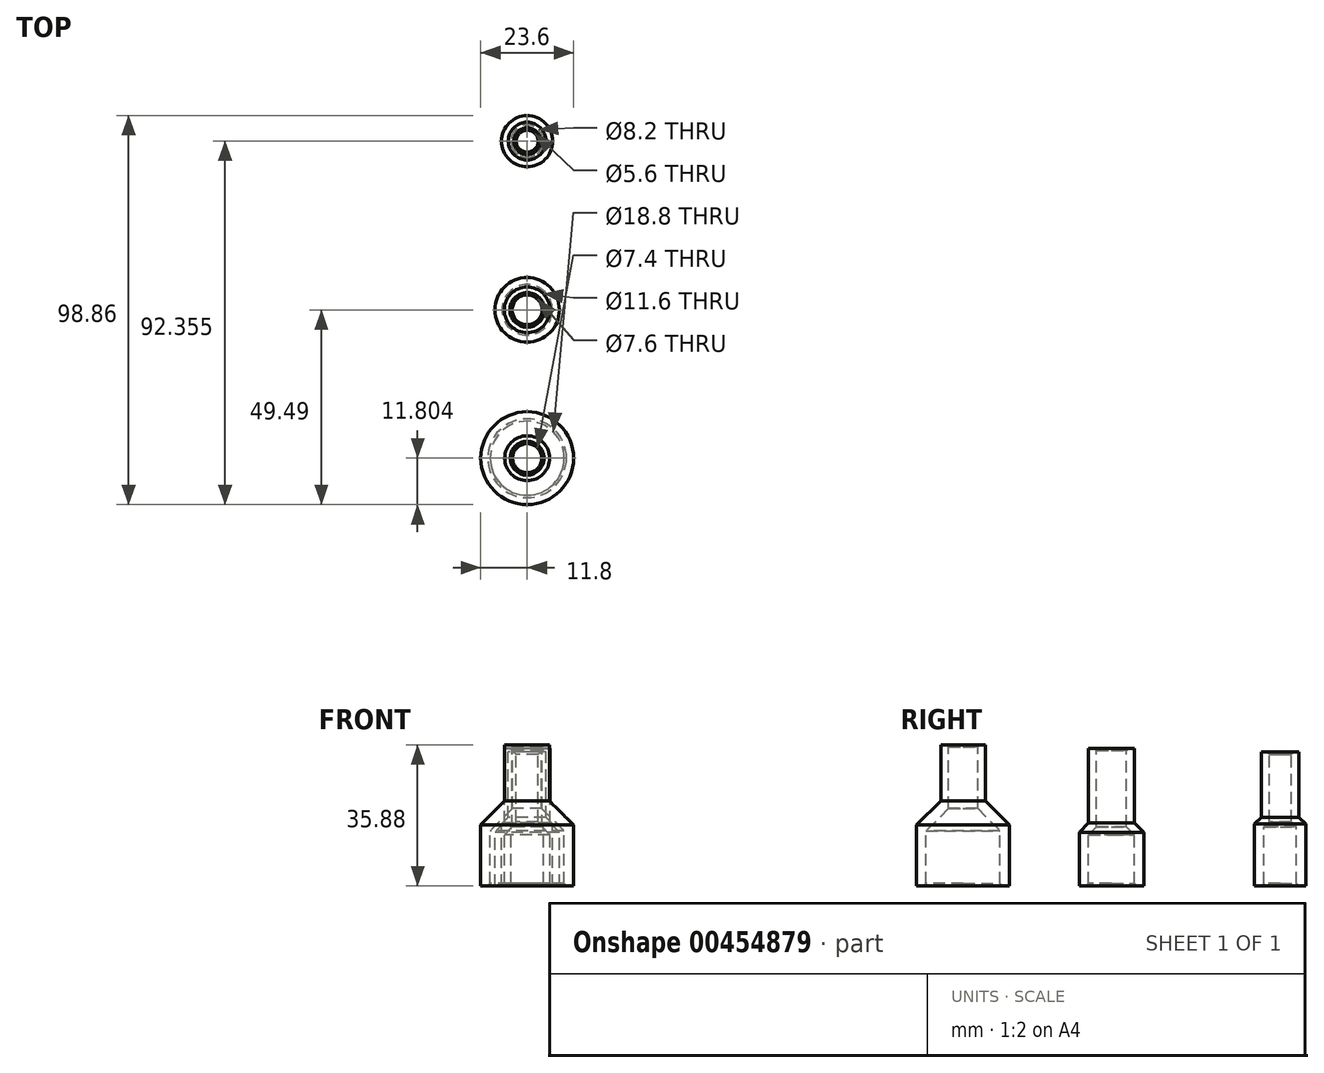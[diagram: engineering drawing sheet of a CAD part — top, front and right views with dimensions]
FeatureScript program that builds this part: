
annotation { "Feature Type Name" : "Feature", "Feature Type Description" : "" }
export const myFeature = defineFeature(function(context is Context, id is Id, definition is map)
    precondition{}
    {
        {
            var Q0;
            Q0=qCreatedBy(makeId("Right.planeOp"),FACE);
            var sketch = newSketch(context, id + "F0", { "sketchPlane" : qUnion([Q0])});
            skLineSegment(sketch, "E0", {"start": v(0, 29.48) * mm, "end": v(0, -19) * mm, "construction": true});
            skLineSegment(sketch, "E1", {"start": v(-5.8, 0) * mm, "end": v(-5.8, 13) * mm});
            skLineSegment(sketch, "E2", {"start": v(-5.8, 13) * mm, "end": v(-3.8, 15) * mm});
            skLineSegment(sketch, "E3", {"start": v(-3.8, 15) * mm, "end": v(-3.8, 34.98) * mm});
            skLineSegment(sketch, "E4", {"start": v(-3.8, 34.98) * mm, "end": v(-5.8, 34.98) * mm});
            skLineSegment(sketch, "E5", {"start": v(-5.8, 34.98) * mm, "end": v(-5.8, 16.05) * mm});
            skLineSegment(sketch, "E6", {"start": v(-5.8, 16.05) * mm, "end": v(-8.2, 13.65) * mm});
            skLineSegment(sketch, "E7", {"start": v(-8.2, 13.65) * mm, "end": v(-8.2, 0) * mm});
            skLineSegment(sketch, "E8", {"start": v(-8.2, 0) * mm, "end": v(-5.8, 0) * mm});
            skLineSegment(sketch, "E9", {"start": v(42.87, 33.76) * mm, "end": v(42.87, -16.37) * mm, "construction": true});
            skLineSegment(sketch, "E10", {"start": v(38.77, 0) * mm, "end": v(38.77, 15) * mm});
            skLineSegment(sketch, "E11", {"start": v(38.77, 15) * mm, "end": v(40.07, 16.3) * mm});
            skLineSegment(sketch, "E12", {"start": v(40.07, 16.3) * mm, "end": v(40.07, 34.07) * mm});
            skLineSegment(sketch, "E13", {"start": v(40.07, 34.07) * mm, "end": v(38.07, 34.07) * mm});
            skLineSegment(sketch, "E14", {"start": v(38.07, 34.07) * mm, "end": v(38.07, 17.4) * mm});
            skLineSegment(sketch, "E15", {"start": v(38.07, 17.4) * mm, "end": v(36.37, 15.7) * mm});
            skLineSegment(sketch, "E16", {"start": v(36.37, 15.7) * mm, "end": v(36.37, 0) * mm});
            skLineSegment(sketch, "E17", {"start": v(36.37, 0) * mm, "end": v(38.77, 0) * mm});
            skLineSegment(sketch, "E18", {"start": v(-47.09, 0) * mm, "end": v(-47.09, 14) * mm});
            skLineSegment(sketch, "E19", {"start": v(-47.09, 14) * mm, "end": v(-41.39, 19.7) * mm});
            skLineSegment(sketch, "E20", {"start": v(-41.39, 19.7) * mm, "end": v(-41.39, 35.88) * mm});
            skLineSegment(sketch, "E21", {"start": v(-41.39, 35.88) * mm, "end": v(-43.39, 35.88) * mm});
            skLineSegment(sketch, "E22", {"start": v(-43.39, 35.88) * mm, "end": v(-43.39, 21.58) * mm});
            skLineSegment(sketch, "E23", {"start": v(-43.39, 21.58) * mm, "end": v(-49.49, 15.48) * mm});
            skLineSegment(sketch, "E24", {"start": v(-49.49, 15.48) * mm, "end": v(-49.49, 0) * mm});
            skLineSegment(sketch, "E25", {"start": v(-49.49, 0) * mm, "end": v(-47.09, 0) * mm});
            skLineSegment(sketch, "E26", {"start": v(-37.69, 38.7) * mm, "end": v(-37.69, -6.54) * mm, "construction": true});
            skSolve(sketch);
        }
        {
            var Q0;
            Q0=makeQuery(id+"F0.imprint","IMPRINT",FACE,{"disambiguationData":[TD([[makeQuery(id+"F0.imprint","IMPRINT",EDGE,{"derivedFrom":sQuery(id+"F0.wireOp",EDGE,"E1")}),1.0]])]});
            var Q1;
            Q1=sQuery(id+"F0.wireOp",EDGE,"E0");
            revolve(context, id + "F1", {"entities" : qUnion([Q0]), "axis" : qUnion([Q1]), "revolveType" : RevolveType.FULL});
        }
        {
            var Q0;
            Q0=makeQuery(id+"F0.imprint","IMPRINT",FACE,{"disambiguationData":[TD([[makeQuery(id+"F0.imprint","IMPRINT",EDGE,{"derivedFrom":sQuery(id+"F0.wireOp",EDGE,"E10")}),1.0]])]});
            var Q1;
            Q1=sQuery(id+"F0.wireOp",EDGE,"E9");
            revolve(context, id + "F2", {"surfaceOperationType" : NewSurfaceOperationType.NEW, "entities" : qUnion([Q0]), "axis" : qUnion([Q1]), "revolveType" : RevolveType.FULL});
        }
        {
            var Q0;
            Q0=makeQuery(id+"F0.imprint","IMPRINT",FACE,{"disambiguationData":[TD([[makeQuery(id+"F0.imprint","IMPRINT",EDGE,{"derivedFrom":sQuery(id+"F0.wireOp",EDGE,"E18")}),1.0]])]});
            var Q1;
            Q1=sQuery(id+"F0.wireOp",EDGE,"E26");
            revolve(context, id + "F3", {"surfaceOperationType" : NewSurfaceOperationType.NEW, "entities" : qUnion([Q0]), "axis" : qUnion([Q1]), "revolveType" : RevolveType.FULL});
        }
        {
            var Q0;
            Q0=makeQuery(id+"F1.opRevolve","SWEPT_EDGE",EDGE,{"disambiguationData":[OSD([sQuery(id+"F0.wireOp",EDGE,"E1"),sQuery(id+"F0.wireOp",EDGE,"E8")])]});
            var Q1;
            Q1=makeQuery(id+"F2.opRevolve","SWEPT_EDGE",EDGE,{"disambiguationData":[OSD([sQuery(id+"F0.wireOp",EDGE,"E10"),sQuery(id+"F0.wireOp",EDGE,"E17")])]});
            var Q2;
            Q2=makeQuery(id+"F2.opRevolve","SWEPT_EDGE",EDGE,{"disambiguationData":[OSD([sQuery(id+"F0.wireOp",EDGE,"E12"),sQuery(id+"F0.wireOp",EDGE,"E13")])]});
            var Q3;
            Q3=makeQuery(id+"F1.opRevolve","SWEPT_EDGE",EDGE,{"disambiguationData":[OSD([sQuery(id+"F0.wireOp",EDGE,"E3"),sQuery(id+"F0.wireOp",EDGE,"E4")])]});
            var Q4;
            Q4=makeQuery(id+"F3.opRevolve","SWEPT_EDGE",EDGE,{"disambiguationData":[OSD([sQuery(id+"F0.wireOp",EDGE,"E20"),sQuery(id+"F0.wireOp",EDGE,"E21")])]});
            var Q5;
            Q5=makeQuery(id+"F3.opRevolve","SWEPT_EDGE",EDGE,{"disambiguationData":[OSD([sQuery(id+"F0.wireOp",EDGE,"E18"),sQuery(id+"F0.wireOp",EDGE,"E25")])]});
            chamfer(context, id + "F4", {"entities" : qUnion([Q0, Q1, Q2, Q3, Q4, Q5]), "width" : 0.6 * mm, "tangentPropagation" : true});
        }
    });
